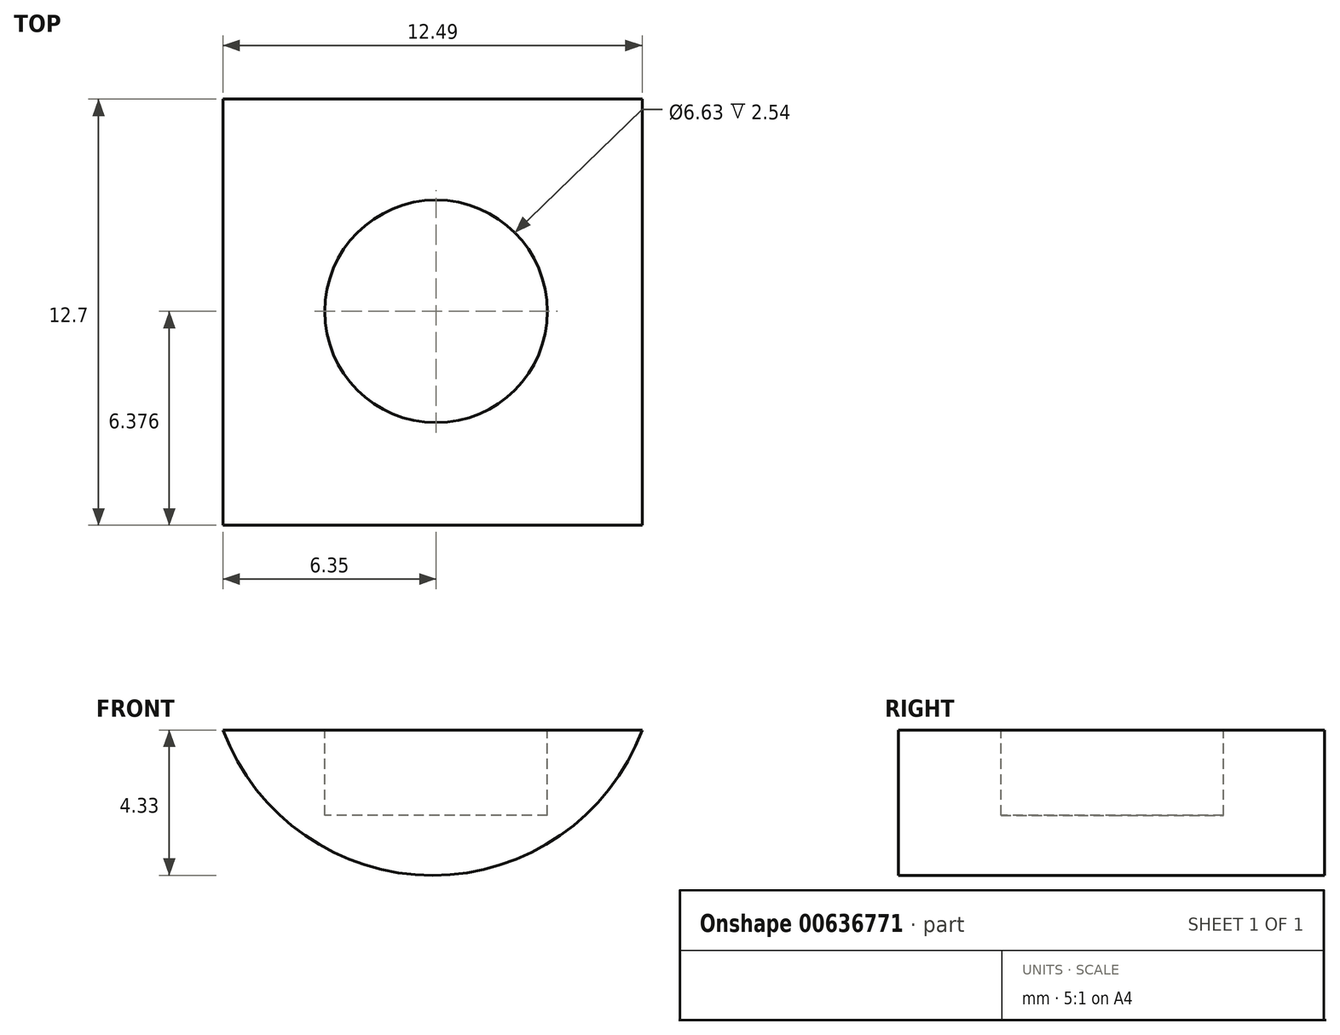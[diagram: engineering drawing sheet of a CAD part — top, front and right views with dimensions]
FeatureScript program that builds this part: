
annotation { "Feature Type Name" : "Feature", "Feature Type Description" : "" }
export const myFeature = defineFeature(function(context is Context, id is Id, definition is map)
    precondition{}
    {
        {
            var Q0;
            Q0=qCreatedBy(makeId("Front.planeOp"),FACE);
            var sketch = newSketch(context, id + "F0", { "sketchPlane" : qUnion([Q0])});
            skArc(sketch, "E0", {"start": v(-6.35, 0) * mm, "mid": v(-0.1, -4.33) * mm, "end": v(6.14, 0) * mm});
            skLineSegment(sketch, "E1", {"start": v(-6.35, 0) * mm, "end": v(-1.76, 0) * mm});
            skLineSegment(sketch, "E2", {"start": v(6.14, 0) * mm, "end": v(1.58, 0) * mm});
            skLineSegment(sketch, "E3", {"start": v(1.58, 0) * mm, "end": v(-1.76, 0) * mm});
            skSolve(sketch);
        }
        {
            var Q0;
            Q0 = qSketchRegion(id + "F0", true);
            extrude(context, id + "F1", {"entities" : qUnion([Q0]), "depth" : 12.7 * mm, "offsetDistance" : 25.4 * mm});
        }
        {
            var Q0;
            Q0=makeQuery(id+"F1.opExtrude","SWEPT_FACE",FACE,{"disambiguationData":[OSD([sQuery(id+"F0.wireOp",EDGE,"E1"),sQuery(id+"F0.wireOp",EDGE,"E2"),sQuery(id+"F0.wireOp",EDGE,"E3")])]});
            var sketch = newSketch(context, id + "F2", { "sketchPlane" : qUnion([Q0])});
            skCircle(sketch, "E4", {"center": v(0, -6.32) * mm, "radius": 3.32 * mm});
            skSolve(sketch);
        }
        {
            var Q0;
            Q0 = qSketchRegion(id + "F2", true);
            extrude(context, id + "F3", {"entities" : qUnion([Q0]), "operationType" : NewBodyOperationType.REMOVE, "oppositeDirection" : true, "depth" : 2.54 * mm, "offsetDistance" : 25.4 * mm});
        }
    });
